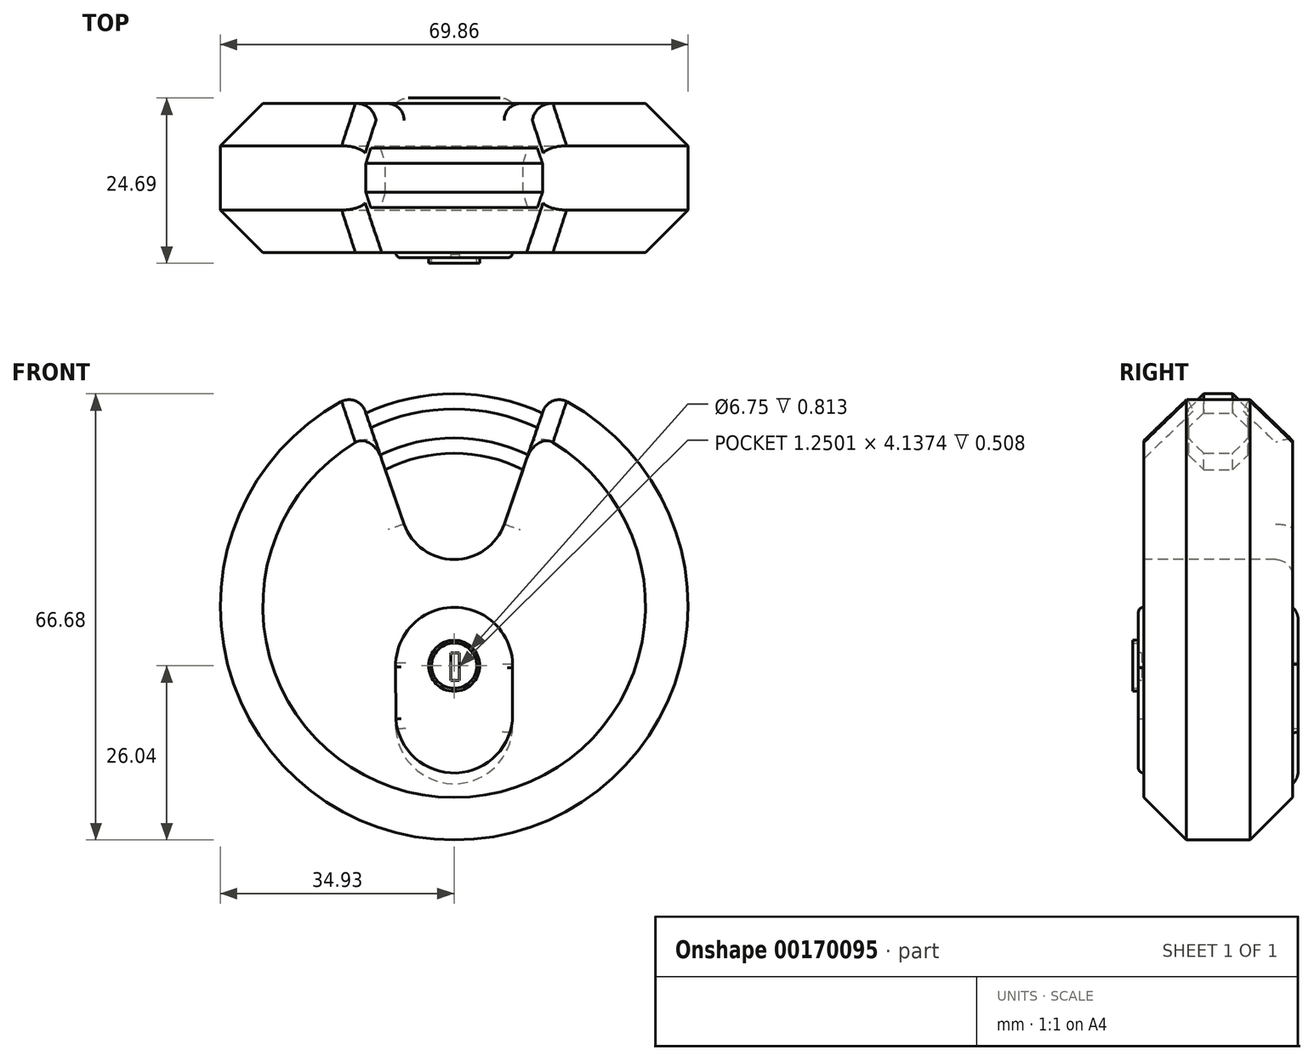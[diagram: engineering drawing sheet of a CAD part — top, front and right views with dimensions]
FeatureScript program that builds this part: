
annotation { "Feature Type Name" : "Feature", "Feature Type Description" : "" }
export const myFeature = defineFeature(function(context is Context, id is Id, definition is map)
    precondition{}
    {
        {
            var Q0;
            Q0=qCreatedBy(makeId("Front.planeOp"),FACE);
            var sketch = newSketch(context, id + "F0", { "sketchPlane" : qUnion([Q0])});
            skCircle(sketch, "E0", {"center": v(0, 0) * mm, "radius": 34.93 * mm});
            skSolve(sketch);
        }
        {
            var Q0;
            Q0 = qSketchRegion(id + "F0", true);
            extrude(context, id + "F1", {"entities" : qUnion([Q0]), "depth" : 22.25 * mm});
        }
        {
            var Q0;
            Q0=makeQuery(id+"F1.opExtrude","CAP_EDGE",EDGE,{"disambiguationData":[OSD([sQuery(id+"F0.wireOp",EDGE,"E0")])],"isStart":false});
            var Q1;
            Q1=makeQuery(id+"F1.opExtrude","CAP_EDGE",EDGE,{"disambiguationData":[OSD([sQuery(id+"F0.wireOp",EDGE,"E0")])],"isStart":true});
            chamfer(context, id + "F2", {"entities" : qUnion([Q0, Q1]), "width" : 6.35 * mm, "tangentPropagation" : true});
        }
        {
            var Q0;
            Q0=makeQuery(id+"F1.opExtrude","CAP_FACE",FACE,{"disambiguationData":[OSD([sQuery(id+"F0.wireOp",EDGE,"E0")])],"isStart":false});
            var sketch = newSketch(context, id + "F3", { "sketchPlane" : qUnion([Q0])});
            skLineSegment(sketch, "E1", {"start": v(7.47, 12.28) * mm, "end": v(18.23, 43.5) * mm});
            skLineSegment(sketch, "E2", {"start": v(18.23, 43.5) * mm, "end": v(0, 43.5) * mm});
            skLineSegment(sketch, "E3.MirrorCS", {"start": v(-7.47, 12.28) * mm, "end": v(-18.23, 43.5) * mm});
            skLineSegment(sketch, "E4", {"start": v(0, 43.5) * mm, "end": v(-18.23, 43.5) * mm});
            skArc(sketch, "E5", {"start": v(-7.47, 12.28) * mm, "mid": v(-4.58, 8.44) * mm, "end": v(0, 6.98) * mm});
            skArc(sketch, "E6.MirrorCS", {"start": v(7.47, 12.28) * mm, "mid": v(4.58, 8.44) * mm, "end": v(0, 6.98) * mm});
            skPoint(sketch, "E7.orphan", {"position": v(-7.47, 12.28) * mm});
            skPoint(sketch, "E8.orphan", {"position": v(7.47, 12.28) * mm});
            skLineSegment(sketch, "E9", {"start": v(-14.23, 31.9) * mm, "end": v(-14.23, 55.24) * mm});
            skLineSegment(sketch, "E10", {"start": v(14.6, 32.97) * mm, "end": v(14.6, 60.03) * mm});
            skSolve(sketch);
        }
        {
            var Q0;
            Q0 = qSketchRegion(id + "F3", true);
            extrude(context, id + "F4", {"entities" : qUnion([Q0]), "operationType" : NewBodyOperationType.REMOVE, "endBound" : BoundingType.THROUGH_ALL, "oppositeDirection" : true, "depth" : 25.4 * mm});
        }
        {
            var Q0;
            Q0=qCreatedBy(makeId("Front.planeOp"),FACE);
            cPlane(context, id + "F5", {"entities" : qUnion([Q0]), "cplaneType" : CPlaneType.OFFSET, "offset" : 11.13 * mm, "width" : 152.4 * mm, "height" : 152.4 * mm});
        }
        {
            var Q0;
            Q0=qCreatedBy(id+"F5.planeOp",FACE);
            var sketch = newSketch(context, id + "F6", { "sketchPlane" : qUnion([Q0])});
            skCircle(sketch, "E11", {"center": v(0, 0) * mm, "radius": 22.86 * mm});
            skCircle(sketch, "E12", {"center": v(0, 0) * mm, "radius": 31.75 * mm});
            skSolve(sketch);
        }
        {
            var Q0;
            Q0 = qSketchRegion(id + "F6", true);
            extrude(context, id + "F7", {"entities" : qUnion([Q0]), "operationType" : NewBodyOperationType.ADD, "depth" : 4.44 * mm});
        }
        {
            var Q0;
            Q0=makeQuery(id+"F7.opExtrude","CAP_FACE",FACE,{"disambiguationData":[OSD([sQuery(id+"F6.wireOp",EDGE,"E11"),sQuery(id+"F6.wireOp",EDGE,"E12")])],"isStart":true});
            extrude(context, id + "F8", {"entities" : qUnion([Q0]), "operationType" : NewBodyOperationType.ADD, "depth" : 4.44 * mm});
        }
        {
            var Q0;
            Q0=makeQuery(id+"F4.boolean.opBoolean","INTERSECT",EDGE,{"derivedFrom":[makeQuery(id+"F1.opExtrude","CAP_FACE",FACE,{"disambiguationData":[OSD([sQuery(id+"F0.wireOp",EDGE,"E0")])],"isStart":true}),makeQuery(id+"F4.opExtrude","SWEPT_FACE",FACE,{"disambiguationData":[OSD([sQuery(id+"F3.wireOp",EDGE,"E3.MirrorCS")])]})]});
            var Q1;
            Q1=makeQuery(id+"F4.boolean.opBoolean","INTERSECT",EDGE,{"derivedFrom":[makeQuery(id+"F1.opExtrude","CAP_FACE",FACE,{"disambiguationData":[OSD([sQuery(id+"F0.wireOp",EDGE,"E0")])],"isStart":true}),makeQuery(id+"F4.opExtrude","SWEPT_FACE",FACE,{"disambiguationData":[OSD([sQuery(id+"F3.wireOp",EDGE,"E5")])]})]});
            var Q2;
            {var subQ0=sQuery(id+"F0.wireOp",EDGE,"E0");Q2=makeQuery(id+"F4.boolean.opBoolean","INTERSECT",EDGE,{"derivedFrom":[makeQuery(id+"F2.opChamfer","BLEND_FACE",FACE,{"disambiguationData":[OSD([subQ0]),TDD([makeQuery(id+"F1.opExtrude","CAP_EDGE",EDGE,{"disambiguationData":[OSD([subQ0])],"isStart":true})])]}),makeQuery(id+"F4.opExtrude","SWEPT_FACE",FACE,{"disambiguationData":[OSD([sQuery(id+"F3.wireOp",EDGE,"E3.MirrorCS")])]})]});}
            var Q3;
            Q3=makeQuery(id+"F4.boolean.opBoolean","INTERSECT",EDGE,{"derivedFrom":[makeQuery(id+"F1.opExtrude","SWEPT_FACE",FACE,{"disambiguationData":[OSD([sQuery(id+"F0.wireOp",EDGE,"E0")])]}),makeQuery(id+"F4.opExtrude","SWEPT_FACE",FACE,{"disambiguationData":[OSD([sQuery(id+"F3.wireOp",EDGE,"E3.MirrorCS")])]})]});
            var Q4;
            {var subQ0=sQuery(id+"F0.wireOp",EDGE,"E0");Q4=makeQuery(id+"F4.boolean.opBoolean","INTERSECT",EDGE,{"derivedFrom":[makeQuery(id+"F2.opChamfer","BLEND_FACE",FACE,{"disambiguationData":[OSD([subQ0]),TDD([makeQuery(id+"F1.opExtrude","CAP_EDGE",EDGE,{"disambiguationData":[OSD([subQ0])],"isStart":false})])]}),makeQuery(id+"F4.opExtrude","SWEPT_FACE",FACE,{"disambiguationData":[OSD([sQuery(id+"F3.wireOp",EDGE,"E3.MirrorCS")])]})]});}
            var Q5;
            Q5=makeQuery(id+"F4.boolean.opBoolean","INTERSECT",EDGE,{"derivedFrom":[makeQuery(id+"F1.opExtrude","CAP_FACE",FACE,{"disambiguationData":[OSD([sQuery(id+"F0.wireOp",EDGE,"E0")])],"isStart":true}),makeQuery(id+"F4.opExtrude","SWEPT_FACE",FACE,{"disambiguationData":[OSD([sQuery(id+"F3.wireOp",EDGE,"E1")])]})]});
            var Q6;
            {var subQ0=sQuery(id+"F0.wireOp",EDGE,"E0");Q6=makeQuery(id+"F4.boolean.opBoolean","INTERSECT",EDGE,{"derivedFrom":[makeQuery(id+"F2.opChamfer","BLEND_FACE",FACE,{"disambiguationData":[OSD([subQ0]),TDD([makeQuery(id+"F1.opExtrude","CAP_EDGE",EDGE,{"disambiguationData":[OSD([subQ0])],"isStart":true})])]}),makeQuery(id+"F4.opExtrude","SWEPT_FACE",FACE,{"disambiguationData":[OSD([sQuery(id+"F3.wireOp",EDGE,"E1")])]})]});}
            var Q7;
            Q7=makeQuery(id+"F4.boolean.opBoolean","INTERSECT",EDGE,{"derivedFrom":[makeQuery(id+"F1.opExtrude","SWEPT_FACE",FACE,{"disambiguationData":[OSD([sQuery(id+"F0.wireOp",EDGE,"E0")])]}),makeQuery(id+"F4.opExtrude","SWEPT_FACE",FACE,{"disambiguationData":[OSD([sQuery(id+"F3.wireOp",EDGE,"E1")])]})]});
            var Q8;
            {var subQ0=sQuery(id+"F0.wireOp",EDGE,"E0");Q8=makeQuery(id+"F4.boolean.opBoolean","INTERSECT",EDGE,{"derivedFrom":[makeQuery(id+"F2.opChamfer","BLEND_FACE",FACE,{"disambiguationData":[OSD([subQ0]),TDD([makeQuery(id+"F1.opExtrude","CAP_EDGE",EDGE,{"disambiguationData":[OSD([subQ0])],"isStart":false})])]}),makeQuery(id+"F4.opExtrude","SWEPT_FACE",FACE,{"disambiguationData":[OSD([sQuery(id+"F3.wireOp",EDGE,"E1")])]})]});}
            var Q9;
            Q9=makeQuery(id+"F4.boolean.opBoolean","COPY",EDGE,{"derivedFrom":makeQuery(id+"F4.opExtrude","CAP_EDGE",EDGE,{"disambiguationData":[OSD([sQuery(id+"F3.wireOp",EDGE,"E1")])],"isStart":true})});
            var Q10;
            Q10=makeQuery(id+"F4.boolean.opBoolean","COPY",EDGE,{"derivedFrom":makeQuery(id+"F4.opExtrude","CAP_EDGE",EDGE,{"disambiguationData":[OSD([sQuery(id+"F3.wireOp",EDGE,"E6.MirrorCS")])],"isStart":true})});
            var Q11;
            Q11=makeQuery(id+"F4.boolean.opBoolean","COPY",EDGE,{"derivedFrom":makeQuery(id+"F4.opExtrude","CAP_EDGE",EDGE,{"disambiguationData":[OSD([sQuery(id+"F3.wireOp",EDGE,"E3.MirrorCS")])],"isStart":true})});
            fillet(context, id + "F9", {"entities" : qUnion([Q0, Q1, Q2, Q3, Q4, Q5, Q6, Q7, Q8, Q9, Q10, Q11]), "radius" : 2.54 * mm, "tangentPropagation" : true, "allowEdgeOverflow" : false});
        }
        {
            var Q0;
            Q0=makeQuery(id+"F8.opExtrude","CAP_EDGE",EDGE,{"disambiguationData":[OSD([sQuery(id+"F6.wireOp",EDGE,"E12")])],"isStart":false});
            var Q1;
            Q1=makeQuery(id+"F8.opExtrude","CAP_EDGE",EDGE,{"disambiguationData":[OSD([sQuery(id+"F6.wireOp",EDGE,"E11")])],"isStart":false});
            var Q2;
            Q2=makeQuery(id+"F7.opExtrude","CAP_EDGE",EDGE,{"disambiguationData":[OSD([sQuery(id+"F6.wireOp",EDGE,"E12")])],"isStart":false});
            var Q3;
            Q3=makeQuery(id+"F7.opExtrude","CAP_EDGE",EDGE,{"disambiguationData":[OSD([sQuery(id+"F6.wireOp",EDGE,"E11")])],"isStart":false});
            chamfer(context, id + "F10", {"entities" : qUnion([Q0, Q1, Q2, Q3]), "width" : 2.3 * mm, "tangentPropagation" : true});
        }
        {
            var Q0;
            Q0=makeQuery(id+"F1.opExtrude","CAP_FACE",FACE,{"disambiguationData":[OSD([sQuery(id+"F0.wireOp",EDGE,"E0")])],"isStart":false});
            var sketch = newSketch(context, id + "F11", { "sketchPlane" : qUnion([Q0])});
            skCircle(sketch, "E13", {"center": v(0, -8.9) * mm, "radius": 3.81 * mm});
            skCircle(sketch, "E14", {"center": v(0, -8.9) * mm, "radius": 3.38 * mm});
            skSolve(sketch);
        }
        {
            var Q0;
            Q0 = qSketchRegion(id + "F11", true);
            var Q1;
            Q1=makeQuery(id+"F11.imprint","IMPRINT",FACE,{"disambiguationData":[TD([[makeQuery(id+"F11.imprint","IMPRINT",EDGE,{"derivedFrom":sQuery(id+"F11.wireOp",EDGE,"NNx4AbBP-AO2Y-3cQk-WaHm-wAXFZq1lfLIv.bottom")}),-1.0]])]});
            extrude(context, id + "F12", {"entities" : qUnion([Q0, Q1]), "operationType" : NewBodyOperationType.ADD, "depth" : 0.81 * mm});
        }
        {
            var Q0;
            {var subQ1=sQuery(id+"F3.wireOp",EDGE,"E1");var subQ2=sQuery(id+"F0.wireOp",EDGE,"E0");Q0=makeQuery(id+"F12.boolean.opBoolean","SPLIT",FACE,{"disambiguationData":[TD([makeQuery(id+"F9.opFillet","BLEND_FACE",FACE,{"disambiguationData":[OSD([subQ1])]})])],"derivedFrom":makeQuery(id+"F1.opExtrude","CAP_FACE",FACE,{"disambiguationData":[OSD([subQ2])],"isStart":false})});}
            var sketch = newSketch(context, id + "F13", { "sketchPlane" : qUnion([Q0])});
            skCircle(sketch, "E15", {"center": v(0, -8.9) * mm, "radius": 8.74 * mm});
            skArc(sketch, "E16", {"start": v(-8.71, -16.85) * mm, "mid": v(0.34, -24.9) * mm, "end": v(8.74, -16.17) * mm});
            skLineSegment(sketch, "E17", {"start": v(8.73, -9.22) * mm, "end": v(8.74, -16.17) * mm});
            skLineSegment(sketch, "E18", {"start": v(-8.74, -8.79) * mm, "end": v(-8.71, -16.85) * mm});
            skSolve(sketch);
        }
        {
            var Q0;
            Q0 = qSketchRegion(id + "F13", true);
            var Q1;
            Q1=makeQuery(id+"F12.opExtrude","CAP_FACE",FACE,{"disambiguationData":[OSD([sQuery(id+"F11.wireOp",EDGE,"E13"),sQuery(id+"F11.wireOp",EDGE,"E14")])],"isStart":false});
            extrude(context, id + "F14", {"entities" : qUnion([Q0, Q1]), "operationType" : NewBodyOperationType.ADD, "depth" : 0.81 * mm});
        }
        {
            var Q0;
            Q0=makeQuery(id+"F14.opExtrude","CAP_EDGE",EDGE,{"disambiguationData":[OSD([sQuery(id+"F13.wireOp",EDGE,"E15")])],"isStart":false});
            var Q1;
            Q1=makeQuery(id+"F14.opExtrude","CAP_EDGE",EDGE,{"disambiguationData":[OSD([sQuery(id+"F13.wireOp",EDGE,"05j7Pmjw-j5Ho-mupO-dRyi-KTPBA9o8NZKG")])],"isStart":false});
            var Q2;
            Q2=makeQuery(id+"F14.opExtrude","CAP_EDGE",EDGE,{"disambiguationData":[OSD([sQuery(id+"F13.wireOp",EDGE,"E16")])],"isStart":false});
            fillet(context, id + "F15", {"entities" : qUnion([Q0, Q1, Q2]), "radius" : 0.81 * mm, "tangentPropagation" : true, "allowEdgeOverflow" : false});
        }
        {
            var Q0;
            Q0=makeQuery(id+"F14.boolean.opBoolean","SPLIT",FACE,{"disambiguationData":[TD([makeQuery(id+"F14.opExtrude","SWEPT_FACE",FACE,{"disambiguationData":[OSD([sQuery(id+"F11.wireOp",EDGE,"E14")])]})])],"derivedFrom":makeQuery(id+"F14.opExtrude","CAP_FACE",FACE,{"disambiguationData":[OSD([sQuery(id+"F13.wireOp",EDGE,"E15"),sQuery(id+"F13.wireOp",EDGE,"E16"),sQuery(id+"F13.wireOp",EDGE,"05j7Pmjw-j5Ho-mupO-dRyi-KTPBA9o8NZKG"),sQuery(id+"F13.wireOp",EDGE,"E17")])],"isStart":false})});
            var sketch = newSketch(context, id + "F16", { "sketchPlane" : qUnion([Q0])});
            skLineSegment(sketch, "E19.bottom", {"start": v(-0.5, -6.94) * mm, "end": v(0.74, -6.94) * mm});
            skLineSegment(sketch, "E19.top", {"start": v(-0.5, -11.07) * mm, "end": v(0.74, -11.07) * mm});
            skLineSegment(sketch, "E19.left", {"start": v(-0.5, -6.94) * mm, "end": v(-0.5, -11.07) * mm});
            skLineSegment(sketch, "E19.right", {"start": v(0.74, -6.94) * mm, "end": v(0.74, -11.07) * mm});
            skSolve(sketch);
        }
        {
            var Q0;
            Q0 = qSketchRegion(id + "F16", true);
            extrude(context, id + "F17", {"entities" : qUnion([Q0]), "operationType" : NewBodyOperationType.REMOVE, "oppositeDirection" : true, "depth" : 0.5 * mm});
        }
        {
            var Q0;
            Q0=makeQuery(id+"F1.opExtrude","CAP_FACE",FACE,{"disambiguationData":[OSD([sQuery(id+"F0.wireOp",EDGE,"E0")])],"isStart":true});
            var sketch = newSketch(context, id + "F18", { "sketchPlane" : qUnion([Q0])});
            skSolve(sketch);
        }
        {
            var Q0;
            {var subQ0=sQuery(id+"F0.wireOp",EDGE,"E0");var subQ1=makeQuery(id+"F1.opExtrude","CAP_FACE",FACE,{"disambiguationData":[OSD([subQ0])],"isStart":true});var subQ5=makeQuery(id+"F1.opExtrude","CAP_EDGE",EDGE,{"disambiguationData":[OSD([subQ0])],"isStart":true});Q0=makeQuery(id+"F18.imprint","IMPRINT",FACE,{"disambiguationData":[TD([[makeQuery(id+"F18.imprint","IMPRINT",EDGE,{"derivedFrom":makeQuery(id+"F2.opChamfer","BLEND_EDGE",EDGE,{"blendedFrom":[subQ5,subQ1],"blendedInto":[subQ1]})}),1.0]])]});}
            var sketch = newSketch(context, id + "F19", { "sketchPlane" : qUnion([Q0])});
            skArc(sketch, "E20", {"start": v(8.72, -8.4) * mm, "mid": v(-0.15, -0.15) * mm, "end": v(-8.74, -8.7) * mm});
            skArc(sketch, "E21", {"start": v(-8.67, -18.9) * mm, "mid": v(0.31, -26.51) * mm, "end": v(8.72, -18.27) * mm});
            skLineSegment(sketch, "E22", {"start": v(-8.74, -8.7) * mm, "end": v(-8.67, -18.9) * mm});
            skLineSegment(sketch, "E23", {"start": v(8.72, -8.4) * mm, "end": v(8.72, -18.27) * mm});
            skSolve(sketch);
        }
        {
            var Q0;
            Q0 = qSketchRegion(id + "F19", true);
            extrude(context, id + "F20", {"entities" : qUnion([Q0]), "operationType" : NewBodyOperationType.ADD, "depth" : 0.81 * mm});
        }
        {
            var Q0;
            Q0=makeQuery(id+"F20.opExtrude","CAP_EDGE",EDGE,{"disambiguationData":[OSD([sQuery(id+"F19.wireOp",EDGE,"E22")])],"isStart":false});
            var Q1;
            Q1=makeQuery(id+"F20.opExtrude","CAP_EDGE",EDGE,{"disambiguationData":[OSD([sQuery(id+"F19.wireOp",EDGE,"E20")])],"isStart":false});
            var Q2;
            Q2=makeQuery(id+"F20.opExtrude","CAP_EDGE",EDGE,{"disambiguationData":[OSD([sQuery(id+"F19.wireOp",EDGE,"E21")])],"isStart":false});
            var Q3;
            Q3=makeQuery(id+"F20.opExtrude","CAP_EDGE",EDGE,{"disambiguationData":[OSD([sQuery(id+"F19.wireOp",EDGE,"E23")])],"isStart":false});
            fillet(context, id + "F21", {"entities" : qUnion([Q0, Q1, Q2, Q3]), "radius" : 2.54 * mm, "tangentPropagation" : true, "allowEdgeOverflow" : false});
        }
    });
